# Revit family: Drain_Vertical_Expansion_Joint-Zurn-Z190
name_source: partatom
category: Plumbing Fixtures
units: mm (PartAtom-declared; Revit-internal decimal feet)

## family parameters
Always vertical = Yes
Cut with Voids When Loaded = No
Maintain Annotation Orientation = No
OmniClass Number = 23.45.55.21
OmniClass Title = Drains (Wastes)
Part Type = Normal
Room Calculation Point = No
Round Connector Dimension = Use Radius
Shared = No
Work Plane-Based = No

## types (7) — shared parameters
Assembly Code = D2040100
CW Connection = No
Default Elevation = 25 "
Description = VERTICAL EXPANSION JOINT
HW Connection = No
Main Material = Iron - Zurn - Cast - Painted - Blue
Manufacturer = Zurn Water, LLC
Manufacturer Brand = Zurn
Model = Z190
Modified Date = 11/21/2025
Sleeve = Bronze - Zurn - Polished
URL = www.zurn.com
Vent Connection = No
WFU = 1
Waste Connection = Yes
zero-valued in all types: CWFU, HWFU

## per-type parameters (varying)
| type | 10 | 2 | 3 | 4 | 6 | 8 | Approx.Wt. Lbs | Inlet Connector | L | L1 | Nominal Diameter_A | O | O1 | Product Documentation Link | Product Installation Sheet | Product Page URL | Product data url | Screw | Type Comments |
| ZRB190-10IP | Yes | No | No | No | No | No |  | 5 " | 5.089 " | 5.61 " | 10 " | 6.48 " | 5.874 " | https://files.zurn.com | https://files.zurn.com | https://www.zurn.com | https://www.bimobject.com | Stainless Steel_Zurn_Polished |  |
| ZRB190-8IP | No | No | No | No | No | Yes |  | 4 " | 5.089 " | 4.853 " | 8 " | 5.606 " | 4.724 " | https://files.zurn.com | https://files.zurn.com | https://www.zurn.com | https://www.bimobject.com | Stainless Steel_Zurn_Polished |  |
| ZRB190-6IP | No | No | No | No | Yes | No | 25 | 3 " | 3.24 " | 3.988 " | 6 " | 4.606 " | 4.724 " | https://files.zurn.com | https://files.zurn.com | https://www.zurn.com | https://www.bimobject.com | Stainless Steel_Zurn_Polished |  |
| ZRB190-4IP | No | No | No | Yes | No | No |  | 2 " | 2.217 " | 2.906 " | 4 " | 3.358 " | 2.559 " | https://files.zurn.com | https://files.zurn.com | https://www.zurn.com | https://www.bimobject.com | Stainless Steel_Zurn_Polished |  |
| ZRB190-3IP | No | No | Yes | No | No | No |  | 1.5 " | 1.705 " | 2.48 " | 3 " | 2.858 " | 1.969 " | http://www.zurn.com |  | http://www.zurn.com | https://bimobject.com | Steel - Zurn - Stainless - Type |  |
| ZRB190-2IP | No | Yes | No | No | No | No | 8 | 1 " | 1.197 " | 2.039 " | 2 " | 2.358 " | 1.378 " | https://files.zurn.com | https://files.zurn.com | https://www.zurn.com | https://www.bimobject.com | Stainless Steel_Zurn_Polished | Z190-2 Inch-Threaded Outlet |
| ZRB190-2NH | No | Yes | No | No | No | No | 8 | 1 " | 1.197 " | 2.039 " | 2 " | 2.358 " | 1.378 " | https://files.zurn.com | https://files.zurn.com | https://www.zurn.com | https://www.bimobject.com | Stainless Steel_Zurn_Polished | Z190-2 Inch-Threaded Outlet |

## geometry (parser evidence)
native form markers: Sweep x8
no freeform markers — native parametric forms only
